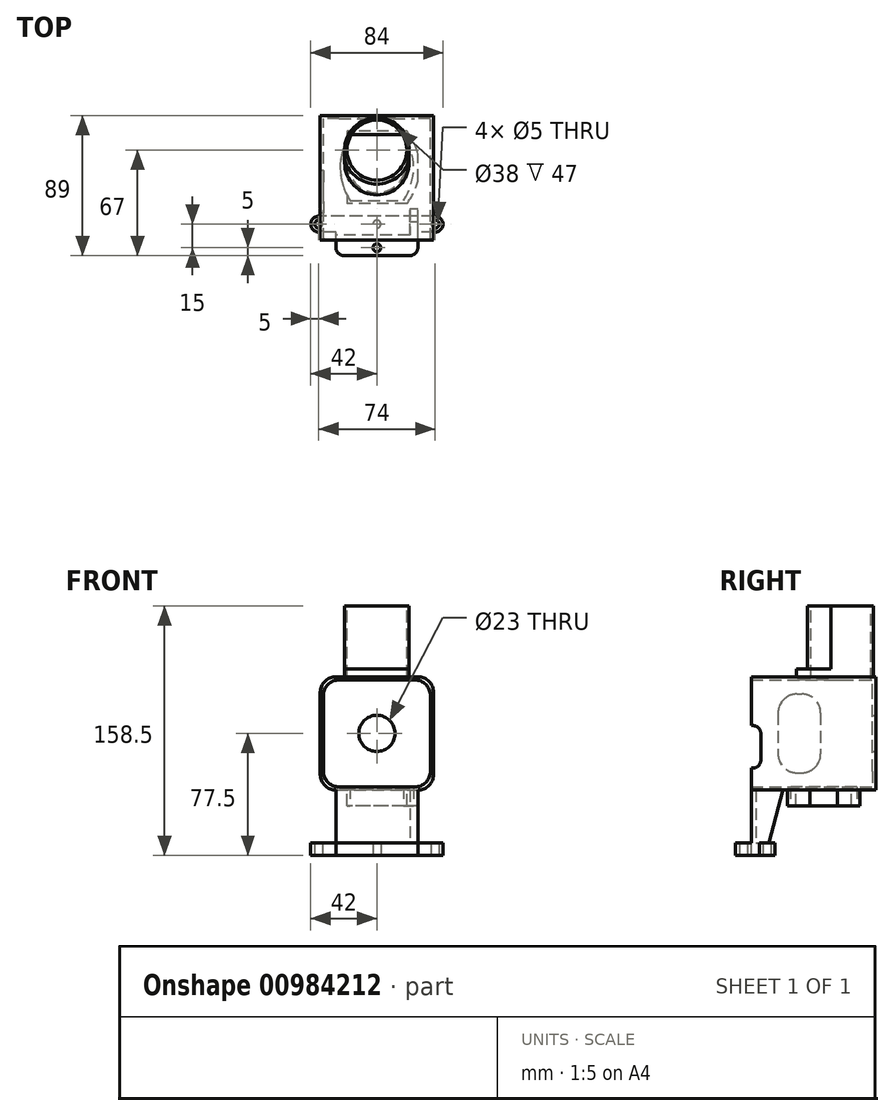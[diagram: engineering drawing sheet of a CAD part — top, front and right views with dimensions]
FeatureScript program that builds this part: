
annotation { "Feature Type Name" : "Feature", "Feature Type Description" : "" }
export const myFeature = defineFeature(function(context is Context, id is Id, definition is map)
    precondition{}
    {
        {
            var Q0;
            Q0=qCreatedBy(makeId("Front.planeOp"),FACE);
            var sketch = newSketch(context, id + "F0", { "sketchPlane" : qUnion([Q0])});
            skLineSegment(sketch, "E0.bottom", {"start": v(-24, -34) * mm, "end": v(24, -34) * mm});
            skLineSegment(sketch, "E0.top", {"start": v(-24, 34) * mm, "end": v(24, 34) * mm});
            skLineSegment(sketch, "E0.left", {"start": v(-34, -24) * mm, "end": v(-34, 24) * mm});
            skLineSegment(sketch, "E0.right", {"start": v(34, -24) * mm, "end": v(34, 24) * mm});
            skPoint(sketch, "E0.middle", {"position": v(0, 0) * mm});
            skLineSegment(sketch, "E1.bottom", {"start": v(-26, 36) * mm, "end": v(26, 36) * mm});
            skLineSegment(sketch, "E1.top", {"start": v(-26, -36) * mm, "end": v(26, -36) * mm});
            skLineSegment(sketch, "E1.left", {"start": v(-36, 26) * mm, "end": v(-36, -26) * mm});
            skLineSegment(sketch, "E1.right", {"start": v(36, 26) * mm, "end": v(36, -26) * mm});
            skCircle(sketch, "E2", {"center": v(0, 0) * mm, "radius": 11.5 * mm});
            skPoint(sketch, "E3.visualSharp", {"position": v(-36, 36) * mm});
            skArc(sketch, "E3.filletArc", {"start": v(-26, 36) * mm, "mid": v(-33.07, 33.07) * mm, "end": v(-36, 26) * mm});
            skPoint(sketch, "E4.visualSharp", {"position": v(-34, 34) * mm});
            skArc(sketch, "E4.filletArc", {"start": v(-24, 34) * mm, "mid": v(-31.07, 31.07) * mm, "end": v(-34, 24) * mm});
            skPoint(sketch, "E5.visualSharp", {"position": v(34, 34) * mm});
            skArc(sketch, "E5.filletArc", {"start": v(34, 24) * mm, "mid": v(31.07, 31.07) * mm, "end": v(24, 34) * mm});
            skPoint(sketch, "E6.visualSharp", {"position": v(36, 36) * mm});
            skArc(sketch, "E6.filletArc", {"start": v(36, 26) * mm, "mid": v(33.07, 33.07) * mm, "end": v(26, 36) * mm});
            skPoint(sketch, "E7.visualSharp", {"position": v(-34, -34) * mm});
            skArc(sketch, "E7.filletArc", {"start": v(-34, -24) * mm, "mid": v(-31.07, -31.07) * mm, "end": v(-24, -34) * mm});
            skPoint(sketch, "E8.visualSharp", {"position": v(-36, -36) * mm});
            skArc(sketch, "E8.filletArc", {"start": v(-36, -26) * mm, "mid": v(-33.07, -33.07) * mm, "end": v(-26, -36) * mm});
            skPoint(sketch, "E9.visualSharp", {"position": v(34, -34) * mm});
            skArc(sketch, "E9.filletArc", {"start": v(24, -34) * mm, "mid": v(31.07, -31.07) * mm, "end": v(34, -24) * mm});
            skPoint(sketch, "E10.visualSharp", {"position": v(36, -36) * mm});
            skArc(sketch, "E10.filletArc", {"start": v(26, -36) * mm, "mid": v(33.07, -33.07) * mm, "end": v(36, -26) * mm});
            skSolve(sketch);
        }
        {
            var Q0;
            Q0=makeQuery(id+"F0.imprint","IMPRINT",FACE,{"disambiguationData":[TD([[makeQuery(id+"F0.imprint","IMPRINT",EDGE,{"derivedFrom":sQuery(id+"F0.wireOp",EDGE,"E0.bottom")}),1.0]])]});
            var Q1;
            Q1=makeQuery(id+"F0.imprint","IMPRINT",FACE,{"disambiguationData":[TD([[makeQuery(id+"F0.imprint","IMPRINT",EDGE,{"derivedFrom":sQuery(id+"F0.wireOp",EDGE,"E0.bottom")}),-1.0]])]});
            extrude(context, id + "F1", {"entities" : qUnion([Q0, Q1]), "depth" : 2 * mm, "offsetDistance" : 25 * mm});
        }
        {
            var Q0;
            Q0=makeQuery(id+"F1.opExtrude","CAP_FACE",FACE,{"disambiguationData":[OSD([sQuery(id+"F0.wireOp",EDGE,"E1.bottom"),sQuery(id+"F0.wireOp",EDGE,"E1.top"),sQuery(id+"F0.wireOp",EDGE,"E1.left"),sQuery(id+"F0.wireOp",EDGE,"E1.right"),sQuery(id+"F0.wireOp",EDGE,"E2"),sQuery(id+"F0.wireOp",EDGE,"E3.filletArc"),sQuery(id+"F0.wireOp",EDGE,"E6.filletArc"),sQuery(id+"F0.wireOp",EDGE,"E8.filletArc"),sQuery(id+"F0.wireOp",EDGE,"E10.filletArc")])],"isStart":false});
            var sketch = newSketch(context, id + "F2", { "sketchPlane" : qUnion([Q0])});
            skLineSegment(sketch, "E11", {"start": v(-26, 36) * mm, "end": v(26, 36) * mm});
            skLineSegment(sketch, "E12", {"start": v(36, 26) * mm, "end": v(36, -26) * mm});
            skLineSegment(sketch, "E13", {"start": v(26, -36) * mm, "end": v(-26, -36) * mm});
            skLineSegment(sketch, "E14", {"start": v(-36, -26) * mm, "end": v(-36, 26) * mm});
            skLineSegment(sketch, "E15.bottom", {"start": v(-24, -34) * mm, "end": v(24, -34) * mm});
            skLineSegment(sketch, "E15.top", {"start": v(-24, 34) * mm, "end": v(24, 34) * mm});
            skLineSegment(sketch, "E15.left", {"start": v(-34, -24) * mm, "end": v(-34, 24) * mm});
            skLineSegment(sketch, "E15.right", {"start": v(34, -24) * mm, "end": v(34, 24) * mm});
            skPoint(sketch, "E15.middle", {"position": v(0, 0) * mm});
            skPoint(sketch, "E16.visualSharp", {"position": v(-34, 34) * mm});
            skArc(sketch, "E16.filletArc", {"start": v(-24, 34) * mm, "mid": v(-31.07, 31.07) * mm, "end": v(-34, 24) * mm});
            skPoint(sketch, "E17.visualSharp", {"position": v(34, 34) * mm});
            skArc(sketch, "E17.filletArc", {"start": v(34, 24) * mm, "mid": v(31.07, 31.07) * mm, "end": v(24, 34) * mm});
            skPoint(sketch, "E18.visualSharp", {"position": v(34, -34) * mm});
            skArc(sketch, "E18.filletArc", {"start": v(24, -34) * mm, "mid": v(31.07, -31.07) * mm, "end": v(34, -24) * mm});
            skPoint(sketch, "E19.visualSharp", {"position": v(-34, -34) * mm});
            skArc(sketch, "E19.filletArc", {"start": v(-34, -24) * mm, "mid": v(-31.07, -31.07) * mm, "end": v(-24, -34) * mm});
            skSolve(sketch);
        }
        {
            var Q0;
            Q0=makeQuery(id+"F2.imprint","IMPRINT",FACE,{"disambiguationData":[TD([[makeQuery(id+"F2.imprint","IMPRINT",EDGE,{"derivedFrom":sQuery(id+"F2.wireOp",EDGE,"E11")}),-1.0]])]});
            extrude(context, id + "F3", {"entities" : qUnion([Q0]), "operationType" : NewBodyOperationType.ADD, "depth" : 77 * mm, "offsetDistance" : 25 * mm});
        }
        {
            var Q0;
            Q0=makeQuery(id+"F3.boolean.opBoolean","MERGE",FACE,{"derivedFrom":[makeQuery(id+"F1.opExtrude","SWEPT_FACE",FACE,{"disambiguationData":[OSD([sQuery(id+"F0.wireOp",EDGE,"E1.left")])]}),makeQuery(id+"F3.opExtrude","SWEPT_FACE",FACE,{"disambiguationData":[OSD([sQuery(id+"F2.wireOp",EDGE,"E14")])]})]});
            var sketch = newSketch(context, id + "F4", { "sketchPlane" : qUnion([Q0])});
            skPoint(sketch, "E20.visualSharp", {"position": v(-64.19, -30) * mm});
            skLineSegment(sketch, "E21.bottom", {"start": v(50, 25) * mm, "end": v(47, 25) * mm});
            skLineSegment(sketch, "E21.top", {"start": v(50, -25) * mm, "end": v(47, -25) * mm});
            skLineSegment(sketch, "E21.left", {"start": v(62, 13) * mm, "end": v(62, -13) * mm});
            skLineSegment(sketch, "E21.right", {"start": v(35, 13) * mm, "end": v(35, -13) * mm});
            skPoint(sketch, "E21.middle", {"position": v(48.5, 0) * mm});
            skPoint(sketch, "E22.visualSharp", {"position": v(62, -25) * mm});
            skArc(sketch, "E22.filletArc", {"start": v(50, -25) * mm, "mid": v(58.49, -21.49) * mm, "end": v(62, -13) * mm});
            skPoint(sketch, "E23.visualSharp", {"position": v(35, -25) * mm});
            skArc(sketch, "E23.filletArc", {"start": v(35, -13) * mm, "mid": v(38.51, -21.49) * mm, "end": v(47, -25) * mm});
            skPoint(sketch, "E24.visualSharp", {"position": v(35, 25) * mm});
            skArc(sketch, "E24.filletArc", {"start": v(47, 25) * mm, "mid": v(38.51, 21.49) * mm, "end": v(35, 13) * mm});
            skPoint(sketch, "E25.visualSharp", {"position": v(62, 25) * mm});
            skArc(sketch, "E25.filletArc", {"start": v(62, 13) * mm, "mid": v(58.49, 21.49) * mm, "end": v(50, 25) * mm});
            skSolve(sketch);
        }
        {
            var Q0;
            Q0=makeQuery(id+"F4.imprint","IMPRINT",FACE,{"disambiguationData":[TD([[makeQuery(id+"F4.imprint","IMPRINT",EDGE,{"derivedFrom":sQuery(id+"F4.wireOp",EDGE,"E21.bottom")}),1.0]])]});
            extrude(context, id + "F5", {"entities" : qUnion([Q0]), "operationType" : NewBodyOperationType.REMOVE, "oppositeDirection" : true, "depth" : 3 * mm, "offsetDistance" : 25 * mm});
        }
        {
            var Q0;
            Q0=makeQuery(id+"F3.boolean.opBoolean","MERGE",FACE,{"derivedFrom":[makeQuery(id+"F1.opExtrude","SWEPT_FACE",FACE,{"disambiguationData":[OSD([sQuery(id+"F0.wireOp",EDGE,"E1.bottom")])]}),makeQuery(id+"F3.opExtrude","SWEPT_FACE",FACE,{"disambiguationData":[OSD([sQuery(id+"F2.wireOp",EDGE,"E11")])]})]});
            var sketch = newSketch(context, id + "F6", { "sketchPlane" : qUnion([Q0])});
            skPoint(sketch, "E26.middle", {"position": v(0, -26) * mm});
            skArc(sketch, "E27", {"start": v(19, -22) * mm, "mid": v(0, -3) * mm, "end": v(-19, -22) * mm});
            skArc(sketch, "E28", {"start": v(-19, -30) * mm, "mid": v(0, -49) * mm, "end": v(19, -30) * mm});
            skPoint(sketch, "E29.orphan", {"position": v(-19, -49) * mm});
            skPoint(sketch, "E30.orphan", {"position": v(19, -49) * mm});
            skPoint(sketch, "E31.orphan", {"position": v(19, -3) * mm});
            skPoint(sketch, "E32.orphan", {"position": v(-19, -3) * mm});
            skLineSegment(sketch, "E33", {"start": v(19, -30) * mm, "end": v(19, -22) * mm});
            skLineSegment(sketch, "E34", {"start": v(-19, -30) * mm, "end": v(-19, -22) * mm});
            skSolve(sketch);
        }
        {
            var Q0;
            Q0=makeQuery(id+"F6.imprint","IMPRINT",FACE,{"disambiguationData":[TD([[makeQuery(id+"F6.imprint","IMPRINT",EDGE,{"derivedFrom":sQuery(id+"F6.wireOp",EDGE,"E27")}),1.0]])]});
            extrude(context, id + "F7", {"entities" : qUnion([Q0]), "operationType" : NewBodyOperationType.REMOVE, "oppositeDirection" : true, "depth" : 3 * mm, "offsetDistance" : 25 * mm});
        }
        {
            var Q0;
            Q0=makeQuery(id+"F3.boolean.opBoolean","MERGE",FACE,{"derivedFrom":[makeQuery(id+"F1.opExtrude","SWEPT_FACE",FACE,{"disambiguationData":[OSD([sQuery(id+"F0.wireOp",EDGE,"E1.bottom")])]}),makeQuery(id+"F3.opExtrude","SWEPT_FACE",FACE,{"disambiguationData":[OSD([sQuery(id+"F2.wireOp",EDGE,"E11")])]})]});
            var sketch = newSketch(context, id + "F8", { "sketchPlane" : qUnion([Q0])});
            skArc(sketch, "E35", {"start": v(19, -22) * mm, "mid": v(0, -3) * mm, "end": v(-19, -22) * mm});
            skArc(sketch, "E36", {"start": v(-19, -30) * mm, "mid": v(0, -49) * mm, "end": v(19, -30) * mm});
            skLineSegment(sketch, "E37", {"start": v(-19, -30) * mm, "end": v(-19, -22) * mm});
            skLineSegment(sketch, "E38", {"start": v(19, -30) * mm, "end": v(19, -29.7) * mm});
            skArc(sketch, "E39", {"start": v(-20.5, -30) * mm, "mid": v(0, -50.5) * mm, "end": v(20.5, -30) * mm});
            skArc(sketch, "E40", {"start": v(20.5, -22) * mm, "mid": v(0, -1.5) * mm, "end": v(-20.5, -22) * mm});
            skLineSegment(sketch, "E41", {"start": v(20.5, -30) * mm, "end": v(20.5, -22) * mm});
            skLineSegment(sketch, "E42", {"start": v(-20.5, -30) * mm, "end": v(-20.5, -22) * mm});
            skLineSegment(sketch, "E43.trimOffspring", {"start": v(19, -22.3) * mm, "end": v(19, -22) * mm});
            skSolve(sketch);
        }
        {
            var Q0;
            Q0=makeQuery(id+"F8.imprint","IMPRINT",FACE,{"disambiguationData":[TD([[makeQuery(id+"F8.imprint","IMPRINT",EDGE,{"derivedFrom":sQuery(id+"F8.wireOp",EDGE,"E35")}),-1.0]])]});
            var Q1;
            Q1=makeQuery(id+"F8.imprint","IMPRINT",FACE,{"disambiguationData":[TD([[makeQuery(id+"F8.imprint","IMPRINT",EDGE,{"derivedFrom":sQuery(id+"F8.wireOp",EDGE,"E35")}),1.0]])]});
            extrude(context, id + "F9", {"entities" : qUnion([Q0, Q1]), "operationType" : NewBodyOperationType.ADD, "depth" : 5 * mm, "offsetDistance" : 25 * mm});
        }
        {
            var Q0;
            Q0=makeQuery(id+"F3.boolean.opBoolean","MERGE",FACE,{"derivedFrom":[makeQuery(id+"F1.opExtrude","SWEPT_FACE",FACE,{"disambiguationData":[OSD([sQuery(id+"F0.wireOp",EDGE,"E1.bottom")])]}),makeQuery(id+"F3.opExtrude","SWEPT_FACE",FACE,{"disambiguationData":[OSD([sQuery(id+"F2.wireOp",EDGE,"E11")])]})]});
            var sketch = newSketch(context, id + "F10", { "sketchPlane" : qUnion([Q0])});
            skArc(sketch, "E44", {"start": v(20.5, -22) * mm, "mid": v(0, -1.5) * mm, "end": v(-20.5, -22) * mm});
            skArc(sketch, "E45", {"start": v(-20.5, -30) * mm, "mid": v(0, -50.5) * mm, "end": v(20.5, -30) * mm});
            skLineSegment(sketch, "E46", {"start": v(-20.5, -30) * mm, "end": v(-20.5, -22) * mm});
            skLineSegment(sketch, "E47", {"start": v(20.5, -30) * mm, "end": v(20.5, -22) * mm});
            skSolve(sketch);
        }
        {
            var Q0;
            Q0=makeQuery(id+"F10.imprint","IMPRINT",FACE,{"disambiguationData":[TD([[makeQuery(id+"F10.imprint","IMPRINT",EDGE,{"derivedFrom":sQuery(id+"F10.wireOp",EDGE,"E44")}),1.0]])]});
            extrude(context, id + "F11", {"entities" : qUnion([Q0]), "operationType" : NewBodyOperationType.ADD, "depth" : 3 * mm, "offsetDistance" : 25 * mm});
        }
        {
            var Q0;
            Q0=makeQuery(id+"F9.opExtrude","CAP_FACE",FACE,{"disambiguationData":[OSD([sQuery(id+"F8.wireOp",EDGE,"E39"),sQuery(id+"F8.wireOp",EDGE,"E40"),sQuery(id+"F8.wireOp",EDGE,"E41"),sQuery(id+"F8.wireOp",EDGE,"E42")])],"isStart":false});
            var sketch = newSketch(context, id + "F12", { "sketchPlane" : qUnion([Q0])});
            skCircle(sketch, "E48", {"center": v(0, -22) * mm, "radius": 19 * mm});
            skPoint(sketch, "E49.center.orphan", {"position": v(0, -19.52) * mm});
            skPoint(sketch, "E50.center.orphan", {"position": v(0, -18.76) * mm});
            skSolve(sketch);
        }
        {
            var Q0;
            Q0=makeQuery(id+"F12.imprint","IMPRINT",FACE,{"disambiguationData":[TD([[makeQuery(id+"F12.imprint","IMPRINT",EDGE,{"derivedFrom":sQuery(id+"F12.wireOp",EDGE,"E48")}),1.0]])]});
            extrude(context, id + "F13", {"entities" : qUnion([Q0]), "operationType" : NewBodyOperationType.REMOVE, "oppositeDirection" : true, "depth" : 8 * mm, "offsetDistance" : 25 * mm});
        }
        {
            var Q0;
            Q0=makeQuery(id+"F9.opExtrude","CAP_FACE",FACE,{"disambiguationData":[OSD([sQuery(id+"F8.wireOp",EDGE,"E39"),sQuery(id+"F8.wireOp",EDGE,"E40"),sQuery(id+"F8.wireOp",EDGE,"E41"),sQuery(id+"F8.wireOp",EDGE,"E42")])],"isStart":false});
            var sketch = newSketch(context, id + "F14", { "sketchPlane" : qUnion([Q0])});
            skCircle(sketch, "E51", {"center": v(0, -22) * mm, "radius": 19 * mm});
            skCircle(sketch, "E52", {"center": v(0, -22) * mm, "radius": 21.5 * mm});
            skSolve(sketch);
        }
        {
            var Q0;
            Q0=makeQuery(id+"F14.imprint","IMPRINT",FACE,{"disambiguationData":[TD([[makeQuery(id+"F14.imprint","IMPRINT",EDGE,{"derivedFrom":sQuery(id+"F14.wireOp",EDGE,"E51")}),-1.0]])]});
            extrude(context, id + "F15", {"entities" : qUnion([Q0]), "operationType" : NewBodyOperationType.ADD, "depth" : 40 * mm, "offsetDistance" : 25 * mm});
        }
        {
            var Q0;
            Q0=makeQuery(id+"F3.boolean.opBoolean","MERGE",FACE,{"derivedFrom":[makeQuery(id+"F1.opExtrude","SWEPT_FACE",FACE,{"disambiguationData":[OSD([sQuery(id+"F0.wireOp",EDGE,"E1.top")])]}),makeQuery(id+"F3.opExtrude","SWEPT_FACE",FACE,{"disambiguationData":[OSD([sQuery(id+"F2.wireOp",EDGE,"E13")])]})]});
            var sketch = newSketch(context, id + "F16", { "sketchPlane" : qUnion([Q0])});
            skLineSegment(sketch, "E53.bottom", {"start": v(26, 79) * mm, "end": v(-26, 79) * mm});
            skLineSegment(sketch, "E53.top", {"start": v(26, 76) * mm, "end": v(-26, 76) * mm});
            skLineSegment(sketch, "E53.left", {"start": v(26, 79) * mm, "end": v(26, 76) * mm});
            skLineSegment(sketch, "E53.right", {"start": v(-26, 79) * mm, "end": v(-26, 76) * mm});
            skSolve(sketch);
        }
        {
            var Q0;
            Q0=makeQuery(id+"F16.imprint","IMPRINT",FACE,{"disambiguationData":[TD([[makeQuery(id+"F16.imprint","IMPRINT",EDGE,{"derivedFrom":sQuery(id+"F16.wireOp",EDGE,"E53.bottom")}),-1.0]])]});
            extrude(context, id + "F17", {"entities" : qUnion([Q0]), "operationType" : NewBodyOperationType.ADD, "depth" : 38.5 * mm, "offsetDistance" : 25 * mm});
        }
        {
            var Q0;
            Q0=makeQuery(id+"F3.boolean.opBoolean","MERGE",FACE,{"derivedFrom":[makeQuery(id+"F1.opExtrude","SWEPT_FACE",FACE,{"disambiguationData":[OSD([sQuery(id+"F0.wireOp",EDGE,"E1.top")])]}),makeQuery(id+"F3.opExtrude","SWEPT_FACE",FACE,{"disambiguationData":[OSD([sQuery(id+"F2.wireOp",EDGE,"E13")])]})]});
            var sketch = newSketch(context, id + "F18", { "sketchPlane" : qUnion([Q0])});
            skLineSegment(sketch, "E54.bottom", {"start": v(17, 12) * mm, "end": v(-17, 12) * mm});
            skLineSegment(sketch, "E54.top", {"start": v(17, 54) * mm, "end": v(-17, 54) * mm});
            skPoint(sketch, "E54.middle", {"position": v(0, 33) * mm});
            skArc(sketch, "E55", {"start": v(17, 12) * mm, "mid": v(23.33, 33) * mm, "end": v(17, 54) * mm});
            skArc(sketch, "E56", {"start": v(-17, 54) * mm, "mid": v(-23.33, 33) * mm, "end": v(-17, 12) * mm});
            skSolve(sketch);
        }
        {
            var Q0;
            Q0=makeQuery(id+"F18.imprint","IMPRINT",FACE,{"disambiguationData":[TD([[makeQuery(id+"F18.imprint","IMPRINT",EDGE,{"derivedFrom":sQuery(id+"F18.wireOp",EDGE,"E54.bottom")}),-1.0]])]});
            extrude(context, id + "F19", {"entities" : qUnion([Q0]), "operationType" : NewBodyOperationType.REMOVE, "oppositeDirection" : true, "depth" : 3 * mm, "offsetDistance" : 25 * mm});
        }
        {
            var Q0;
            Q0=makeQuery(id+"F3.boolean.opBoolean","MERGE",FACE,{"derivedFrom":[makeQuery(id+"F1.opExtrude","SWEPT_FACE",FACE,{"disambiguationData":[OSD([sQuery(id+"F0.wireOp",EDGE,"E1.top")])]}),makeQuery(id+"F3.opExtrude","SWEPT_FACE",FACE,{"disambiguationData":[OSD([sQuery(id+"F2.wireOp",EDGE,"E13")])]})]});
            var sketch = newSketch(context, id + "F20", { "sketchPlane" : qUnion([Q0])});
            skLineSegment(sketch, "E57.bottom", {"start": v(-17, 12) * mm, "end": v(17, 12) * mm});
            skLineSegment(sketch, "E57.top", {"start": v(-17, 54) * mm, "end": v(17, 54) * mm});
            skPoint(sketch, "E57.middle", {"position": v(0, 33) * mm});
            skPoint(sketch, "E57.middle.positionSnap0", {"position": v(0, 12) * mm});
            skPoint(sketch, "E57.centerSnap0", {"position": v(0, 12) * mm});
            skArc(sketch, "E58", {"start": v(17, 12) * mm, "mid": v(23.33, 33) * mm, "end": v(17, 54) * mm});
            skArc(sketch, "E59", {"start": v(-17, 54) * mm, "mid": v(-23.33, 33) * mm, "end": v(-17, 12) * mm});
            skLineSegment(sketch, "E60.bottom", {"start": v(19, 10) * mm, "end": v(-19, 10) * mm});
            skLineSegment(sketch, "E60.top", {"start": v(19, 56) * mm, "end": v(-19, 56) * mm});
            skLineSegment(sketch, "E60.left", {"start": v(19, 10) * mm, "end": v(19, 56) * mm});
            skLineSegment(sketch, "E60.right", {"start": v(-19, 10) * mm, "end": v(-19, 56) * mm});
            skArc(sketch, "E61", {"start": v(19, 10) * mm, "mid": v(27.02, 33) * mm, "end": v(19, 56) * mm});
            skArc(sketch, "E62", {"start": v(-19, 56) * mm, "mid": v(-27.02, 33) * mm, "end": v(-19, 10) * mm});
            skSolve(sketch);
        }
        {
            var Q0;
            {var subQ1=sQuery(id+"F20.wireOp",EDGE,"E60.left");var subQ7=sQuery(id+"F20.wireOp",EDGE,"E58");var subQ9=makeQuery(id+"F20.imprint","INTERSECT",VERTEX,{"disambiguationData":[OD(0.0)],"derivedFrom":[subQ7,subQ1]});Q0=makeQuery(id+"F20.imprint","IMPRINT",FACE,{"disambiguationData":[TD([[makeQuery(id+"F20.imprint","IMPRINT",EDGE,{"disambiguationData":[TD([[subQ9,-1.0]])],"derivedFrom":subQ7}),-1.0]])]});}
            var Q1;
            {var subQ1=sQuery(id+"F20.wireOp",EDGE,"E57.top");Q1=makeQuery(id+"F20.imprint","IMPRINT",FACE,{"disambiguationData":[TD([[makeQuery(id+"F20.imprint","IMPRINT",EDGE,{"derivedFrom":subQ1}),-1.0]])]});}
            var Q2;
            {var subQ1=sQuery(id+"F20.wireOp",EDGE,"E60.right");var subQ6=sQuery(id+"F20.wireOp",EDGE,"E59");var subQ7=makeQuery(id+"F20.imprint","INTERSECT",VERTEX,{"disambiguationData":[OD(0.0)],"derivedFrom":[subQ6,subQ1]});Q2=makeQuery(id+"F20.imprint","IMPRINT",FACE,{"disambiguationData":[TD([[makeQuery(id+"F20.imprint","IMPRINT",EDGE,{"disambiguationData":[TD([[subQ7,-1.0]])],"derivedFrom":subQ6}),-1.0]])]});}
            var Q3;
            {var subQ2=sQuery(id+"F20.wireOp",EDGE,"E57.bottom");Q3=makeQuery(id+"F20.imprint","IMPRINT",FACE,{"disambiguationData":[TD([[makeQuery(id+"F20.imprint","IMPRINT",EDGE,{"derivedFrom":subQ2}),1.0]])]});}
            extrude(context, id + "F21", {"entities" : qUnion([Q0, Q1, Q2, Q3]), "operationType" : NewBodyOperationType.ADD, "depth" : 10 * mm, "offsetDistance" : 25 * mm});
        }
        {
            var Q0;
            Q0=makeQuery(id+"F17.opExtrude","SWEPT_FACE",FACE,{"disambiguationData":[OSD([sQuery(id+"F16.wireOp",EDGE,"E53.left")])]});
            var sketch = newSketch(context, id + "F22", { "sketchPlane" : qUnion([Q0])});
            skLineSegment(sketch, "E63", {"start": v(-79, -74.5) * mm, "end": v(-69, -74.5) * mm});
            skLineSegment(sketch, "E64", {"start": v(-69, -74.5) * mm, "end": v(-59, -36) * mm});
            skLineSegment(sketch, "E65", {"start": v(-59, -36) * mm, "end": v(-79, -36) * mm});
            skLineSegment(sketch, "E66", {"start": v(-79, -36) * mm, "end": v(-79, -74.5) * mm});
            skSolve(sketch);
        }
        {
            var Q0;
            {var subQ2=sQuery(id+"F22.wireOp",EDGE,"E64");Q0=makeQuery(id+"F22.imprint","IMPRINT",FACE,{"disambiguationData":[TD([[makeQuery(id+"F22.imprint","IMPRINT",EDGE,{"derivedFrom":subQ2}),1.0]])]});}
            var Q1;
            {var subQ0=sQuery(id+"F22.wireOp",EDGE,"E66");Q1=makeQuery(id+"F22.imprint","IMPRINT",FACE,{"disambiguationData":[TD([[makeQuery(id+"F22.imprint","IMPRINT",EDGE,{"derivedFrom":subQ0}),-1.0]])]});}
            extrude(context, id + "F23", {"entities" : qUnion([Q0, Q1]), "operationType" : NewBodyOperationType.ADD, "oppositeDirection" : true, "depth" : 5 * mm, "offsetDistance" : 25 * mm});
        }
        {
            var Q0;
            Q0=makeQuery(id+"F17.opExtrude","SWEPT_FACE",FACE,{"disambiguationData":[OSD([sQuery(id+"F16.wireOp",EDGE,"E53.right")])]});
            var sketch = newSketch(context, id + "F24", { "sketchPlane" : qUnion([Q0])});
            skLineSegment(sketch, "E67", {"start": v(79, -74.5) * mm, "end": v(69, -74.5) * mm});
            skLineSegment(sketch, "E68", {"start": v(69, -74.5) * mm, "end": v(59, -36) * mm});
            skLineSegment(sketch, "E69", {"start": v(59, -36) * mm, "end": v(79, -36) * mm});
            skLineSegment(sketch, "E70", {"start": v(79, -36) * mm, "end": v(79, -74.5) * mm});
            skSolve(sketch);
        }
        {
            var Q0;
            Q0=makeQuery(id+"FvH5MofawmtUx0a_1.boolean.opBoolean","MERGE",FACE,{"derivedFrom":[makeQuery(id+"F23.boolean.opBoolean","MERGE",FACE,{"derivedFrom":[makeQuery(id+"F17.opExtrude","CAP_FACE",FACE,{"disambiguationData":[OSD([sQuery(id+"F16.wireOp",EDGE,"E53.bottom"),sQuery(id+"F16.wireOp",EDGE,"E53.top"),sQuery(id+"F16.wireOp",EDGE,"E53.left"),sQuery(id+"F16.wireOp",EDGE,"E53.right")])],"isStart":false}),makeQuery(id+"F23.opExtrude","SWEPT_FACE",FACE,{"disambiguationData":[OSD([sQuery(id+"F22.wireOp",EDGE,"E63")])]})]}),makeQuery(id+"FvH5MofawmtUx0a_1.opExtrude","SWEPT_FACE",FACE,{"disambiguationData":[OSD([sQuery(id+"F24.wireOp",EDGE,"E67")])]})]});
            var sketch = newSketch(context, id + "F25", { "sketchPlane" : qUnion([Q0])});
            skLineSegment(sketch, "E71.bottom", {"start": v(-26, 79) * mm, "end": v(26, 79) * mm});
            skLineSegment(sketch, "E71.top", {"start": v(-26, 74) * mm, "end": v(26, 74) * mm});
            skLineSegment(sketch, "E71.left", {"start": v(-26, 79) * mm, "end": v(-26, 74) * mm});
            skLineSegment(sketch, "E71.right", {"start": v(26, 79) * mm, "end": v(26, 74) * mm});
            skLineSegment(sketch, "E72.bottom", {"start": v(37, 64) * mm, "end": v(-37, 64) * mm});
            skLineSegment(sketch, "E72.top", {"start": v(37, 74) * mm, "end": v(-37, 74) * mm});
            skPoint(sketch, "E72.middle", {"position": v(0, 69) * mm});
            skCircle(sketch, "E73", {"center": v(37, 69) * mm, "radius": 2.5 * mm});
            skCircle(sketch, "E74", {"center": v(-37, 69) * mm, "radius": 2.5 * mm});
            skCircle(sketch, "E75", {"center": v(0, 69) * mm, "radius": 2.5 * mm});
            skArc(sketch, "E76", {"start": v(37, 64) * mm, "mid": v(42, 69) * mm, "end": v(37, 74) * mm});
            skArc(sketch, "E77", {"start": v(-37, 74) * mm, "mid": v(-42, 69) * mm, "end": v(-37, 64) * mm});
            skPoint(sketch, "E78.orphan", {"position": v(50, 64) * mm});
            skPoint(sketch, "E72.left.end.orphan", {"position": v(50, 74) * mm});
            skPoint(sketch, "E79.orphan", {"position": v(-50, 64) * mm});
            skPoint(sketch, "E80.orphan", {"position": v(-50, 74) * mm});
            skLineSegment(sketch, "E81.bottom", {"start": v(26, 79) * mm, "end": v(-26.03, 79) * mm});
            skLineSegment(sketch, "E81.top", {"start": v(21, 89) * mm, "end": v(-21.03, 89) * mm});
            skLineSegment(sketch, "E81.left", {"start": v(26, 79) * mm, "end": v(26, 84) * mm});
            skLineSegment(sketch, "E81.right", {"start": v(-26.03, 79) * mm, "end": v(-26.03, 84) * mm});
            skPoint(sketch, "E82.visualSharp", {"position": v(26, 89) * mm});
            skArc(sketch, "E82.filletArc", {"start": v(26, 84) * mm, "mid": v(24.54, 87.54) * mm, "end": v(21, 89) * mm});
            skPoint(sketch, "E83.visualSharp", {"position": v(-26.03, 89) * mm});
            skArc(sketch, "E83.filletArc", {"start": v(-21.03, 89) * mm, "mid": v(-24.57, 87.54) * mm, "end": v(-26.03, 84) * mm});
            skCircle(sketch, "E84", {"center": v(0, 84) * mm, "radius": 2.5 * mm});
            skSolve(sketch);
        }
        {
            var Q0;
            Q0=makeQuery(id+"F25.imprint","IMPRINT",FACE,{"disambiguationData":[TD([[makeQuery(id+"F25.imprint","IMPRINT",EDGE,{"derivedFrom":sQuery(id+"F25.wireOp",EDGE,"E72.bottom")}),-1.0]])]});
            var Q1;
            Q1=makeQuery(id+"F25.imprint","IMPRINT",FACE,{"disambiguationData":[TD([[makeQuery(id+"F25.imprint","IMPRINT",EDGE,{"derivedFrom":sQuery(id+"F25.wireOp",EDGE,"E71.bottom")}),-1.0]])]});
            var Q2;
            {var subQ1=sQuery(id+"F22.wireOp",EDGE,"E63");var subQ2=makeQuery(id+"F23.opExtrude","CAP_EDGE",EDGE,{"disambiguationData":[OSD([subQ1])],"isStart":false});Q2=makeQuery(id+"F25.imprint","IMPRINT",FACE,{"disambiguationData":[TD([[makeQuery(id+"F25.imprint","IMPRINT",EDGE,{"derivedFrom":subQ2}),1.0]])]});}
            var Q3;
            {var subQ1=sQuery(id+"F24.wireOp",EDGE,"E67");var subQ2=makeQuery(id+"FvH5MofawmtUx0a_1.opExtrude","CAP_EDGE",EDGE,{"disambiguationData":[OSD([subQ1])],"isStart":false});Q3=makeQuery(id+"F25.imprint","IMPRINT",FACE,{"disambiguationData":[TD([[makeQuery(id+"F25.imprint","IMPRINT",EDGE,{"derivedFrom":subQ2}),-1.0]])]});}
            var Q4;
            {var subQ5=makeQuery(id+"F17.opExtrude","CAP_EDGE",EDGE,{"disambiguationData":[OSD([sQuery(id+"F16.wireOp",EDGE,"E53.top")])],"isStart":false});Q4=makeQuery(id+"F25.imprint","IMPRINT",FACE,{"disambiguationData":[TD([[makeQuery(id+"F25.imprint","IMPRINT",EDGE,{"derivedFrom":subQ5}),1.0]])]});}
            var Q5;
            Q5=makeQuery(id+"F25.imprint","IMPRINT",FACE,{"disambiguationData":[TD([[makeQuery(id+"F25.imprint","IMPRINT",EDGE,{"derivedFrom":sQuery(id+"F25.wireOp",EDGE,"E81.top")}),1.0]])]});
            extrude(context, id + "F26", {"entities" : qUnion([Q0, Q1, Q2, Q3, Q4, Q5]), "operationType" : NewBodyOperationType.ADD, "oppositeDirection" : true, "depth" : 5 * mm, "offsetDistance" : 25 * mm});
        }
        {
            var Q0;
            Q0=makeQuery(id+"F26.boolean.opBoolean","MERGE",FACE,{"derivedFrom":[makeQuery(id+"FvH5MofawmtUx0a_1.boolean.opBoolean","MERGE",FACE,{"derivedFrom":[makeQuery(id+"F23.boolean.opBoolean","MERGE",FACE,{"derivedFrom":[makeQuery(id+"F17.opExtrude","CAP_FACE",FACE,{"disambiguationData":[OSD([sQuery(id+"F16.wireOp",EDGE,"E53.bottom"),sQuery(id+"F16.wireOp",EDGE,"E53.top"),sQuery(id+"F16.wireOp",EDGE,"E53.left"),sQuery(id+"F16.wireOp",EDGE,"E53.right")])],"isStart":false}),makeQuery(id+"F23.opExtrude","SWEPT_FACE",FACE,{"disambiguationData":[OSD([sQuery(id+"F22.wireOp",EDGE,"E63")])]})]}),makeQuery(id+"FvH5MofawmtUx0a_1.opExtrude","SWEPT_FACE",FACE,{"disambiguationData":[OSD([sQuery(id+"F24.wireOp",EDGE,"E67")])]})]}),makeQuery(id+"F26.opExtrude","CAP_FACE",FACE,{"disambiguationData":[OSD([sQuery(id+"F25.wireOp",EDGE,"E71.bottom"),sQuery(id+"F25.wireOp",EDGE,"E71.left"),sQuery(id+"F25.wireOp",EDGE,"E71.right"),sQuery(id+"F25.wireOp",EDGE,"E72.bottom"),sQuery(id+"F25.wireOp",EDGE,"E72.top"),sQuery(id+"F25.wireOp",EDGE,"E73"),sQuery(id+"F25.wireOp",EDGE,"E74"),sQuery(id+"F25.wireOp",EDGE,"E75"),sQuery(id+"F25.wireOp",EDGE,"E76"),sQuery(id+"F25.wireOp",EDGE,"E77")])],"isStart":true})]});
            extrude(context, id + "F27", {"entities" : qUnion([Q0]), "operationType" : NewBodyOperationType.ADD, "depth" : 1 * mm, "offsetDistance" : 25 * mm});
        }
        {
            var Q0;
            Q0=makeQuery(id+"F3.boolean.opBoolean","MERGE",FACE,{"derivedFrom":[makeQuery(id+"F1.opExtrude","SWEPT_FACE",FACE,{"disambiguationData":[OSD([sQuery(id+"F0.wireOp",EDGE,"E1.right")])]}),makeQuery(id+"F3.opExtrude","SWEPT_FACE",FACE,{"disambiguationData":[OSD([sQuery(id+"F2.wireOp",EDGE,"E12")])]})]});
            var sketch = newSketch(context, id + "F28", { "sketchPlane" : qUnion([Q0])});
            skLineSegment(sketch, "E85.bottom", {"start": v(-79, 5) * mm, "end": v(-78, 5) * mm});
            skLineSegment(sketch, "E85.top", {"start": v(-79, -22) * mm, "end": v(-78, -22) * mm});
            skLineSegment(sketch, "E85.left", {"start": v(-79, 5) * mm, "end": v(-79, -22) * mm});
            skLineSegment(sketch, "E85.right", {"start": v(-73, 0) * mm, "end": v(-73, -17) * mm});
            skPoint(sketch, "E86.visualSharp", {"position": v(-73, 5) * mm});
            skArc(sketch, "E86.filletArc", {"start": v(-73, 0) * mm, "mid": v(-74.46, 3.54) * mm, "end": v(-78, 5) * mm});
            skPoint(sketch, "E87.visualSharp", {"position": v(-73, -22) * mm});
            skArc(sketch, "E87.filletArc", {"start": v(-78, -22) * mm, "mid": v(-74.46, -20.54) * mm, "end": v(-73, -17) * mm});
            skSolve(sketch);
        }
        {
            var Q0;
            Q0=makeQuery(id+"F28.imprint","IMPRINT",FACE,{"disambiguationData":[TD([[makeQuery(id+"F28.imprint","IMPRINT",EDGE,{"derivedFrom":sQuery(id+"F28.wireOp",EDGE,"E85.bottom")}),-1.0]])]});
            extrude(context, id + "F29", {"entities" : qUnion([Q0]), "operationType" : NewBodyOperationType.REMOVE, "oppositeDirection" : true, "depth" : 75 * mm, "offsetDistance" : 25 * mm});
        }
        {
            var Q0;
            Q0=makeQuery(id+"F27.opExtrude","CAP_FACE",FACE,{"disambiguationData":[OSD([sQuery(id+"F16.wireOp",EDGE,"E53.bottom"),sQuery(id+"F16.wireOp",EDGE,"E53.top"),sQuery(id+"F16.wireOp",EDGE,"E53.left"),sQuery(id+"F16.wireOp",EDGE,"E53.right"),sQuery(id+"F22.wireOp",EDGE,"E63"),sQuery(id+"F25.wireOp",EDGE,"E71.left"),sQuery(id+"F25.wireOp",EDGE,"E72.bottom"),sQuery(id+"F25.wireOp",EDGE,"E72.top"),sQuery(id+"F25.wireOp",EDGE,"E73"),sQuery(id+"F25.wireOp",EDGE,"E74"),sQuery(id+"F25.wireOp",EDGE,"E75"),sQuery(id+"F25.wireOp",EDGE,"E76"),sQuery(id+"F25.wireOp",EDGE,"E77"),sQuery(id+"F25.wireOp",EDGE,"E81.bottom"),sQuery(id+"F25.wireOp",EDGE,"E81.top"),sQuery(id+"F25.wireOp",EDGE,"E81.left"),sQuery(id+"F25.wireOp",EDGE,"E81.right"),sQuery(id+"F25.wireOp",EDGE,"E82.filletArc"),sQuery(id+"F25.wireOp",EDGE,"E83.filletArc"),sQuery(id+"F25.wireOp",EDGE,"E84")])],"isStart":false});
            extrude(context, id + "F30", {"entities" : qUnion([Q0]), "operationType" : NewBodyOperationType.ADD, "depth" : 2 * mm, "offsetDistance" : 25 * mm});
        }
    });
